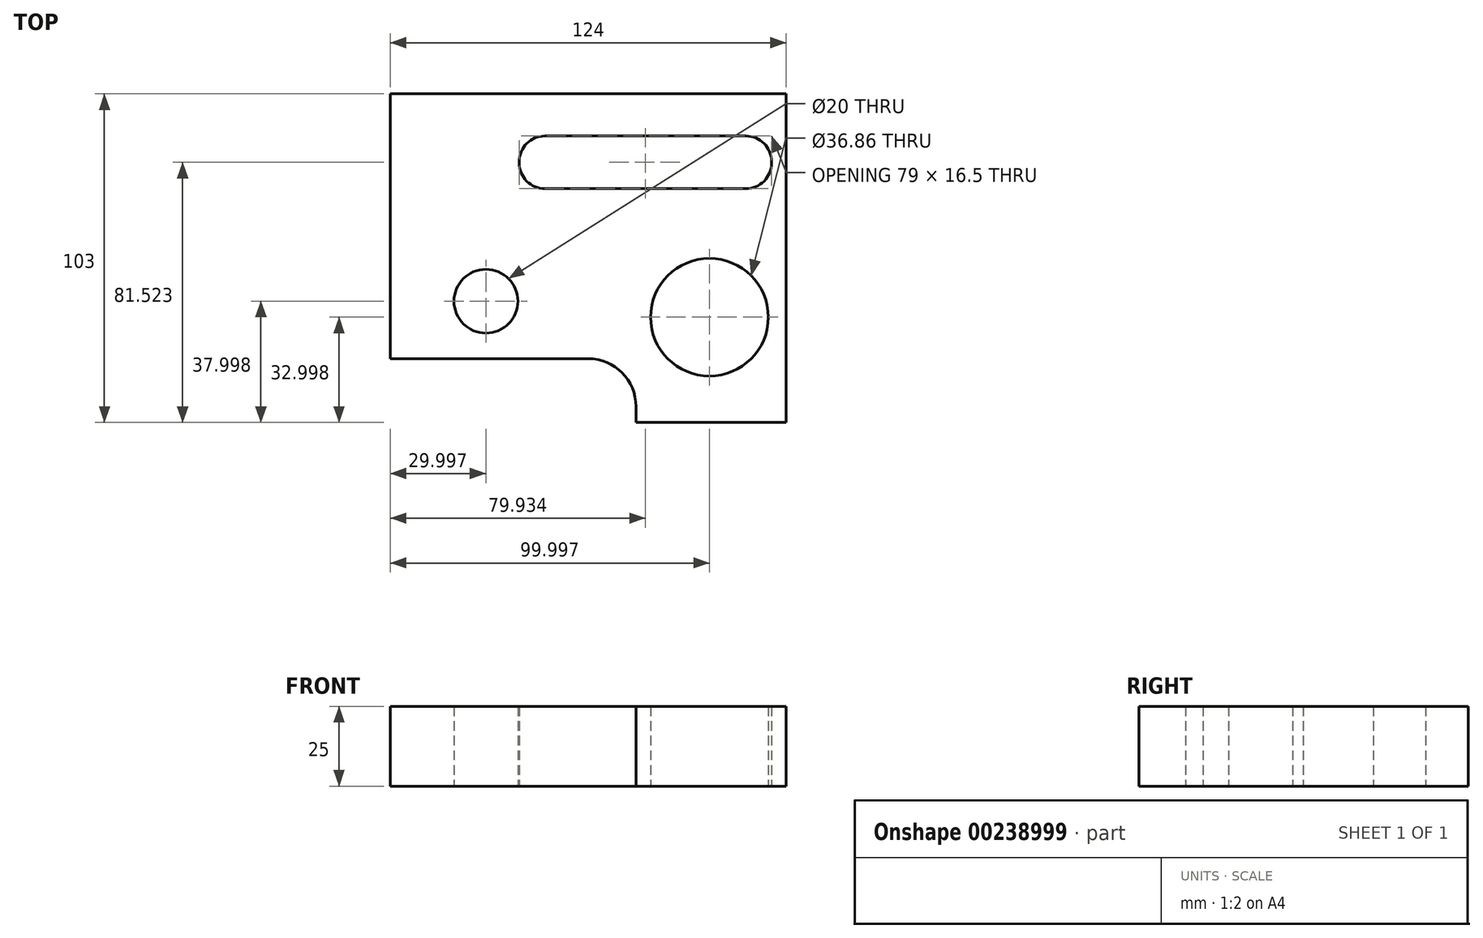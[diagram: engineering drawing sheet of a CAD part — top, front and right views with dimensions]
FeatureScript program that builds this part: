
annotation { "Feature Type Name" : "Feature", "Feature Type Description" : "" }
export const myFeature = defineFeature(function(context is Context, id is Id, definition is map)
    precondition{}
    {
        {
            var Q0;
            Q0=qCreatedBy(makeId("Top.planeOp"),FACE);
            var sketch = newSketch(context, id + "F0", { "sketchPlane" : qUnion([Q0])});
            skLineSegment(sketch, "E0", {"start": v(-60, 52.49) * mm, "end": v(64, 52.49) * mm});
            skLineSegment(sketch, "E1", {"start": v(-60, 52.49) * mm, "end": v(-60, -30.51) * mm});
            skLineSegment(sketch, "E2", {"start": v(-60, -30.51) * mm, "end": v(2, -30.51) * mm});
            skLineSegment(sketch, "E3", {"start": v(64, 52.49) * mm, "end": v(64, -50.51) * mm});
            skLineSegment(sketch, "E4", {"start": v(64, -50.51) * mm, "end": v(17, -50.51) * mm});
            skLineSegment(sketch, "E5", {"start": v(17, -50.51) * mm, "end": v(17, -45.51) * mm});
            skPoint(sketch, "E6.visualSharp", {"position": v(17, -30.51) * mm});
            skArc(sketch, "E6.filletArc", {"start": v(17, -45.51) * mm, "mid": v(12.6, -34.9) * mm, "end": v(2, -30.51) * mm});
            skCircle(sketch, "E7", {"center": v(-30, -12.51) * mm, "radius": 10 * mm});
            skCircle(sketch, "E8", {"center": v(40, -17.51) * mm, "radius": 18.43 * mm});
            skLineSegment(sketch, "E9", {"start": v(51.43, 39.26) * mm, "end": v(-11.57, 39.26) * mm});
            skLineSegment(sketch, "E10", {"start": v(-11.57, 22.76) * mm, "end": v(51.43, 22.76) * mm});
            skLineSegment(sketch, "E11", {"start": v(-19.57, 31.26) * mm, "end": v(-19.57, 30.76) * mm});
            skLineSegment(sketch, "E12", {"start": v(59.43, 31.26) * mm, "end": v(59.43, 30.76) * mm});
            skPoint(sketch, "E13.visualSharp", {"position": v(-19.57, 39.26) * mm});
            skArc(sketch, "E13.filletArc", {"start": v(-11.57, 39.26) * mm, "mid": v(-17.22, 36.92) * mm, "end": v(-19.57, 31.26) * mm});
            skPoint(sketch, "E14.visualSharp", {"position": v(-19.57, 22.76) * mm});
            skArc(sketch, "E14.filletArc", {"start": v(-19.57, 30.76) * mm, "mid": v(-17.22, 25.1) * mm, "end": v(-11.57, 22.76) * mm});
            skPoint(sketch, "E15.visualSharp", {"position": v(59.43, 39.26) * mm});
            skArc(sketch, "E15.filletArc", {"start": v(59.43, 31.26) * mm, "mid": v(57.1, 36.92) * mm, "end": v(51.43, 39.26) * mm});
            skPoint(sketch, "E16.visualSharp", {"position": v(59.43, 22.76) * mm});
            skArc(sketch, "E16.filletArc", {"start": v(51.43, 22.76) * mm, "mid": v(57.1, 25.1) * mm, "end": v(59.43, 30.76) * mm});
            skSolve(sketch);
        }
        {
            var Q0;
            Q0 = qSketchRegion(id + "F0", true);
            extrude(context, id + "F1", {"entities" : qUnion([Q0]), "depth" : 25 * mm});
        }
    });
